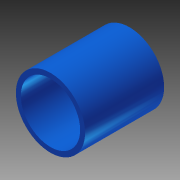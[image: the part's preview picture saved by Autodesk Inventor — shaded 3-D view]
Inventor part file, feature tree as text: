
AUTODESK INVENTOR PART (.ipt)
format: ipt  version: 2012 (Build 160160000, 160)  size: 87,040 bytes
history: native  units: in
note: dims shown in document units (in); Inventor stores cm internally (conversion verified against a paired STEP export)
features: extrude x1, sketch x1
ambient origin geometry x8: Origin, YZ Plane, XZ Plane, XY Plane, X Axis, Y Axis, Z Axis, Center Point
bodies: Solid1 (feature_tree)
feature tree (2):
  extrude  "Extrusion1"  Depth=1.125in
  sketch  "Sketch1"  dims[d0=1.3125in d1=1.125in d2=1.5in d3=0.0in]
